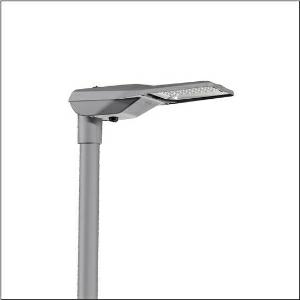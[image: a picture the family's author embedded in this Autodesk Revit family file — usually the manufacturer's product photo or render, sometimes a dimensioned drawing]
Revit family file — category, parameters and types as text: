
# Revit family: streetlight_sl_21_mini___p0_8ab_5xe2r33t08gb_6801
name_source: partatom
category: Lighting Fixtures
units: mm (PartAtom-declared; Revit-internal decimal feet)

## family parameters
Cut with Voids When Loaded = No
Host = Face
Light Source = No
Part Type = Normal
Room Calculation Point = No
Round Connector Dimension = Use Diameter
Shared = No

## types (1)
- --- (1 x LED, 5160 lm, 40.4 W, 3000K)
    Apparent Load = 40 VA
    CIE Flux Codes = 36 71 98 100 100
    Color Rendering = 70
    Color Temperature = 3000K
    Default Elevation = 1800 mm
    Description = Streetlight SL 21 mini, mast luminaire, primary light control with lens, of PMMA, primary optical cover: cover, of toughened safety glass, transparent, light distribution: P0.8aB, light emission: direct distribution, primary light characteristic: asymmetric, installation type: post-top, side-entry, LED, High Power LED, rated luminous flux: 5.160lm, luminous efficacy: 128lm/W, light colour: 730, colour temperature: 3000K, control gear: D4i, control: pre-setting: logarithmic dimming characteristic, flexible luminous flux parameterisation, time-dependent luminous flux control, constant luminous flux control, overheat protection, mains connection: 220..240V, AC, 50/60Hz, start of lifetime: 40W, end of service life: 41W, reduction: 19W, luminaire housing, of diecast aluminium, powder-coated, SITECO metallic grey (DB 702S), corrosivity category C5 high according to DIN EN ISO 12944, multi-level sealing system, sealing non-destructively replaceable, inclination adjustable: 0°, 5°, 10°, 15°, please order mast flange separately, length: 628mm, width: 235mm, height: 110mm, mast flange for spigot size: 42mm (side-entry): 5XC10008XM4, 60/48mm (side-entry/post-top): 5XC10108XM2, 76/60mm (side-entry/post-top): 5XC10108XM1, mounting height: 4..8m, Smart Interface below and above, protection rating (complete): IP66, insulation class (complete): insulation class II (safety insulation), certification: CE, ENEC, ENEC+, VDE, impact resistance: IK10, permissible operating ambient temperature for outdoor applications: -40..+50°C, standard-compliant lighting for roads and squares, packaging unit: 1 piece

Light Distribution: P0.8aB
    Height = 110 mm
    Lamp = 1 x LED
    Lamp Light Flux = 5160 lm
    Lamp Power = 40.4 W
    Lamp count = 1
    Length = 625 mm
    Luminous efficacy = 128 lm/W
    Manufacturer = Siteco
    ModVariant = No
    Model = 5XE2R33T08GB
    Number of Poles = 1
    OnlyDefault = Yes
    Power Factor = 1
    Product Name = Streetlight SL 21 mini | P0.8aB
    Product group = mast luminaire | pylon top
    ProductGroupID = 6100
    Protection Class = Protection class II
    Protection Degree = IP 66
    RLX_Detail_Level = 1
    RLX_Emergency_Light_Flux = 0 lm
    RLX_Emergency_Type = 0
    RLX_Emergency_Type_DB = No
    RlxData = <blob elided: 91897 chars, md5=fbbcc33c>
    Socket = socket
    Standby Power = 0 W
    System Light Flux = 5160 lm
    System Power = 40 W
    Type Comments = factory setting: luminous flux: 100 % | dim-lin: 254 | 812 mA
    Type Image = l_1003514.jpg
    URL = http://relux.com
    VarID = @adj_082339
    Voltage = 0 V
    Weight = 0.00 kg
    Width = 234 mm

## geometry (parser evidence)
native form markers: Blend x4, Sweep x13
no freeform markers — native parametric forms only
